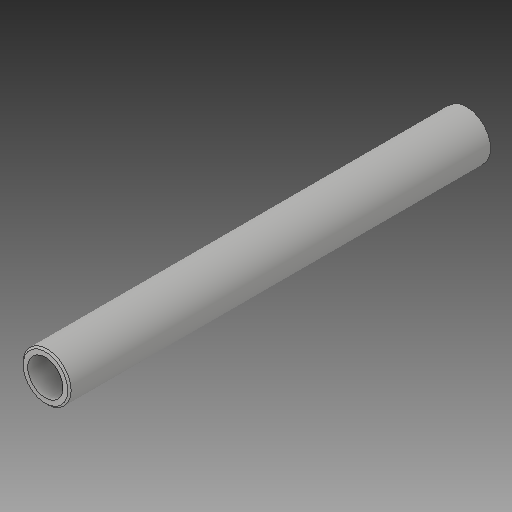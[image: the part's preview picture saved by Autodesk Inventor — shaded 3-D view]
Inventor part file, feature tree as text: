
AUTODESK INVENTOR PART (.ipt)
format: ipt  version: 2018 (Build 220112000, 112)  size: 91,136 bytes
history: native  units: mm
features: extrude x1, chamfer x1, sketch x1
ambient origin geometry x8: Origin, YZ Plane, XZ Plane, XY Plane, X Axis, Y Axis, Z Axis, Center Point
bodies: Solid1 (feature_tree)
feature tree (3):
  extrude  "Extrusion1"  Depth=500.72mm
  chamfer  "Chamfer1"  Distance=500.72mm
  sketch  "Sketch1"  dims[d0=57.2mm d1=41.9mm d2=500.72mm d3=0.0mm d4=2.0mm d5=2.0mm d6=45.0deg]
